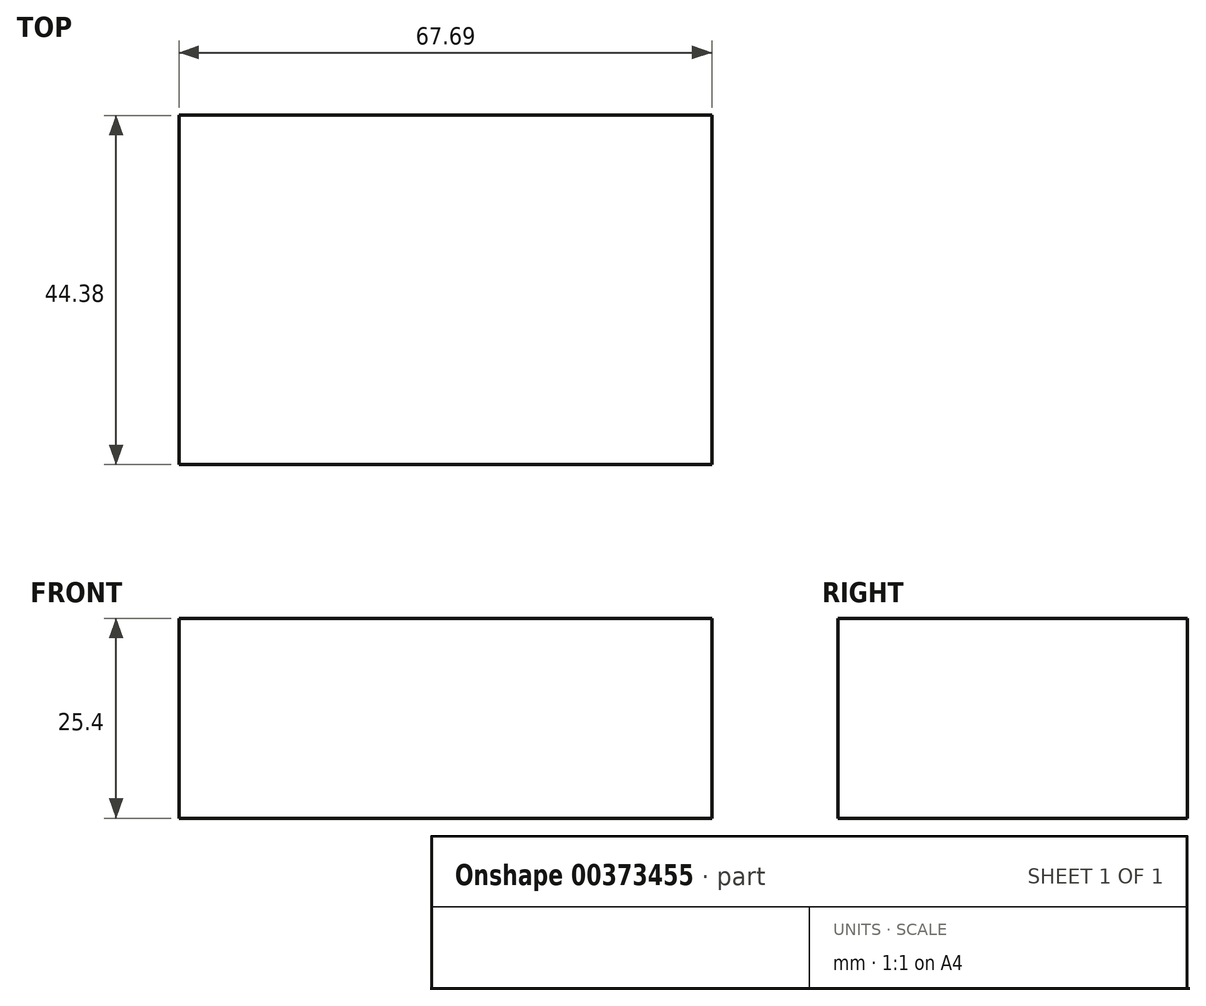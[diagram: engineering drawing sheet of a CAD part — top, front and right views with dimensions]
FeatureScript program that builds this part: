
annotation { "Feature Type Name" : "Feature", "Feature Type Description" : "" }
export const myFeature = defineFeature(function(context is Context, id is Id, definition is map)
    precondition{}
    {
        {
            var Q0;
            Q0=qCreatedBy(makeId("Top.planeOp"),FACE);
            var sketch = newSketch(context, id + "F0", { "sketchPlane" : qUnion([Q0])});
            skLineSegment(sketch, "E0.bottom", {"start": v(0, 0) * mm, "end": v(67.69, 0) * mm});
            skLineSegment(sketch, "E0.top", {"start": v(0, 44.38) * mm, "end": v(67.69, 44.38) * mm});
            skLineSegment(sketch, "E0.left", {"start": v(0, 0) * mm, "end": v(0, 44.38) * mm});
            skLineSegment(sketch, "E0.right", {"start": v(67.69, 0) * mm, "end": v(67.69, 44.38) * mm});
            skSolve(sketch);
        }
        {
            var Q0;
            Q0=makeQuery(id+"F0.imprint","IMPRINT",FACE,{"disambiguationData":[TD([[makeQuery(id+"F0.imprint","IMPRINT",EDGE,{"derivedFrom":sQuery(id+"F0.wireOp",EDGE,"E0.bottom")}),1.0]])]});
            extrude(context, id + "F1", {"entities" : qUnion([Q0]), "depth" : 25.4 * mm});
        }
    });
